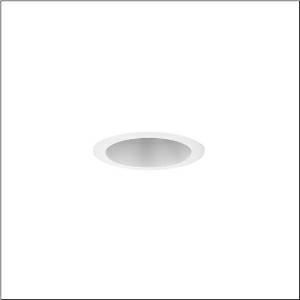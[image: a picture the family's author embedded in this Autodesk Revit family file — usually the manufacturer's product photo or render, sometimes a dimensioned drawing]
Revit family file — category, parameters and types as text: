
# Revit family: lunis_31-l_51dn16ee31b
name_source: partatom
category: Lighting Fixtures
units: mm (PartAtom-declared; Revit-internal decimal feet)

## family parameters
Cut with Voids When Loaded = No
Host = Face
Light Source = No
Part Type = Normal
Room Calculation Point = No
Round Connector Dimension = Use Diameter
Shared = No

## types (1)
- --- (1 x LED, 1550 lm, 12 W, 3000K)
    Apparent Load = 12 VA
    CIE Flux Codes = 76 93 99 100 100
    Color Rendering = 80
    Color Temperature = 3000K
    Default Elevation = 1800 mm
    Description = Lunis 31-L, downlight, light control with reflector, light emission: direct distribution, LED rated luminous flux: 1.550lm, light colour: 830, mains connection: 220..240V, AC/DC, 0/50..60Hz, housing, of aluminium, white, protection rating (complete): IP20, protection rating (on room side): IP54, insulation class (complete): insulation class II (safety insulation), certification: CE, ENEC, packaging unit: 1 piece
    Height = 0 mm  [stored 0 ft]
    Lamp = 1 x LED
    Lamp Light Flux = 1550 lm
    Lamp Power = 12 W
    Lamp count = 1
    Length = 188 mm  [stored 0.616798 ft]
    Luminous efficacy = 129 lm/W
    Manufacturer = Siteco
    ModVariant = No
    Model = 51DN16EE31B
    Mounting Place = Ceiling
    Mounting Type = Recessed
    Number of Poles = 1
    OnlyDefault = Yes
    Power Factor = 1
    Product Name = Lunis 31-L
    Product group = downlight
    ProductGroupID = 401
    Protection Class = Protection class II
    Protection Degree = IP 20
    RLX_Detail_Level = 1
    RLX_Emergency_Light_Flux = 0 lm
    RLX_Emergency_Type = 0
    RLX_Emergency_Type_DB = No
    RlxData = <blob elided: 22577 chars, md5=b1a0eefc>
    Socket = socket
    Standby Power = 0 W
    System Light Flux = 1550 lm
    System Power = 12 W
    Type Comments = individual setting: luminous flux: 100 % | (OFF | ON) | 300 mA
    Type Image = l_1345911.jpg
    URL = http://relux.com
    VarID = @adj_029909
    Voltage = 0 V
    Weight = 0.00 kg
    Width = 0 mm  [stored 0 ft]

note: [stored X ft] marks values corroborated as IEEE doubles in the binary element streams (Revit-internal decimal feet)

## geometry (parser evidence)
native form markers: Blend x4, Sweep x12
no freeform markers — native parametric forms only
